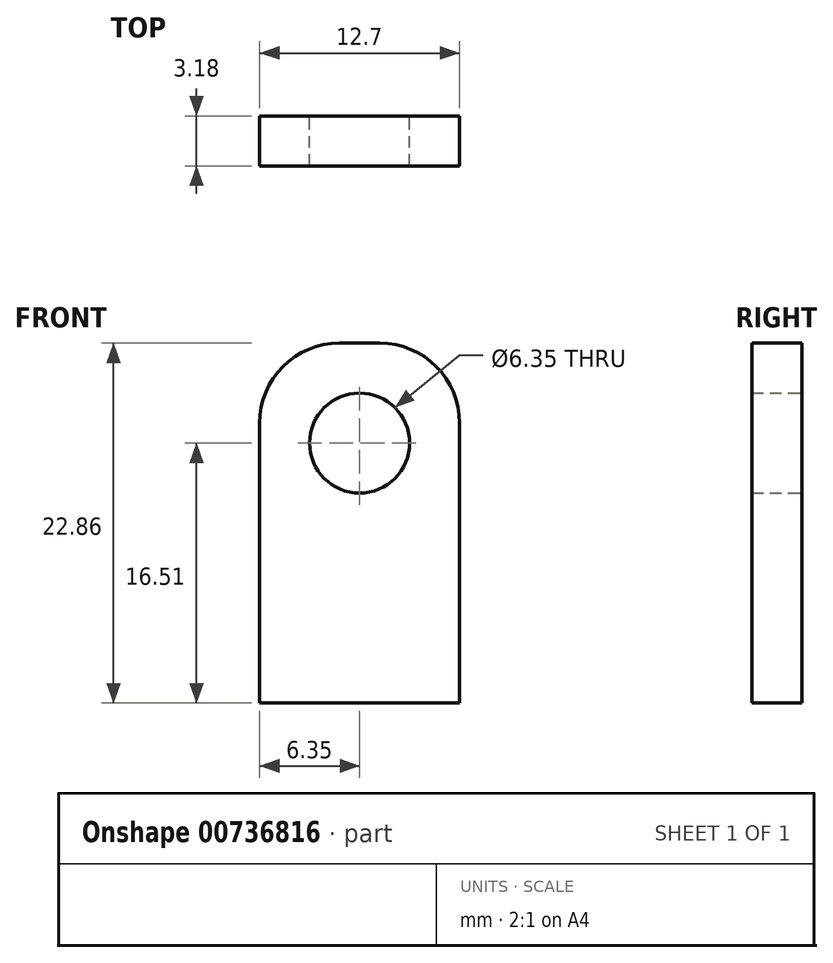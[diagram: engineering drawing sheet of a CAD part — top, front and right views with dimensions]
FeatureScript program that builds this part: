
annotation { "Feature Type Name" : "Feature", "Feature Type Description" : "" }
export const myFeature = defineFeature(function(context is Context, id is Id, definition is map)
    precondition{}
    {
        {
            var Q0;
            Q0=qCreatedBy(makeId("Front.planeOp"),FACE);
            var sketch = newSketch(context, id + "F0", { "sketchPlane" : qUnion([Q0])});
            skLineSegment(sketch, "E0.bottom", {"start": v(0, 0) * mm, "end": v(-12.7, 0) * mm});
            skLineSegment(sketch, "E0.top", {"start": v(0, 22.86) * mm, "end": v(-12.7, 22.86) * mm});
            skLineSegment(sketch, "E0.left", {"start": v(0, 0) * mm, "end": v(0, 22.86) * mm});
            skLineSegment(sketch, "E0.right", {"start": v(-12.7, 0) * mm, "end": v(-12.7, 22.86) * mm});
            skLineSegment(sketch, "E1", {"start": v(-6.35, 0) * mm, "end": v(-6.35, 22.86) * mm});
            skCircle(sketch, "E2", {"center": v(-6.35, 16.51) * mm, "radius": 3.18 * mm});
            skLineSegment(sketch, "E3", {"start": v(-6.35, 19.69) * mm, "end": v(-6.35, 22.86) * mm});
            skSolve(sketch);
        }
        {
            var Q0;
            {var subQ5=sQuery(id+"F0.wireOp",EDGE,"E0.left");Q0=makeQuery(id+"F0.imprint","IMPRINT",FACE,{"disambiguationData":[TD([[makeQuery(id+"F0.imprint","IMPRINT",EDGE,{"derivedFrom":subQ5}),1.0]])]});}
            var Q1;
            {var subQ0=sQuery(id+"F0.wireOp",EDGE,"E0.right");Q1=makeQuery(id+"F0.imprint","IMPRINT",FACE,{"disambiguationData":[TD([[makeQuery(id+"F0.imprint","IMPRINT",EDGE,{"derivedFrom":subQ0}),-1.0]])]});}
            extrude(context, id + "F1", {"entities" : qUnion([Q0, Q1]), "depth" : 3.17 * mm, "offsetDistance" : 25.4 * mm});
        }
        {
            var Q0;
            Q0=makeQuery(id+"F1.opExtrude","SWEPT_EDGE",EDGE,{"disambiguationData":[OSD([sQuery(id+"F0.wireOp",EDGE,"E0.top"),sQuery(id+"F0.wireOp",EDGE,"E0.left")])]});
            fillet(context, id + "F2", {"entities" : qUnion([Q0]), "radius" : 5.08 * mm, "tangentPropagation" : true, "allowEdgeOverflow" : false});
        }
        {
            var Q0;
            Q0=makeQuery(id+"F1.opExtrude","SWEPT_EDGE",EDGE,{"disambiguationData":[OSD([sQuery(id+"F0.wireOp",EDGE,"E0.top"),sQuery(id+"F0.wireOp",EDGE,"E0.right")])]});
            fillet(context, id + "F3", {"entities" : qUnion([Q0]), "radius" : 5.08 * mm, "tangentPropagation" : true, "allowEdgeOverflow" : false});
        }
    });
